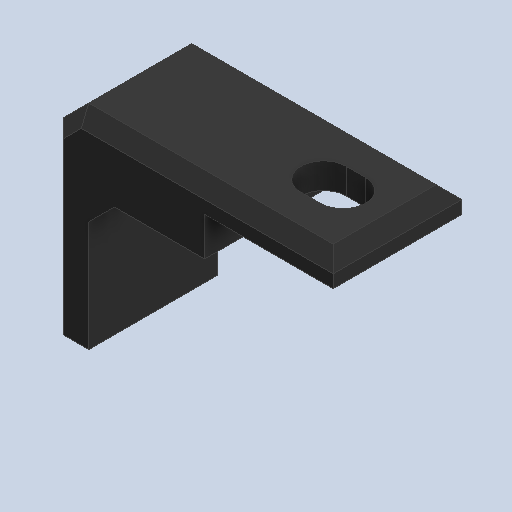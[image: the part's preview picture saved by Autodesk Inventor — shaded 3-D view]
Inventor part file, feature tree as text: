
AUTODESK INVENTOR PART (.ipt)
format: ipt  version: 2024.2 (Build 282272000, 272)  size: 308,736 bytes
history: native  units: mm
features: chamfer x3, extrude x2, sketch x1
ambient origin geometry x8: Origin, YZ Plane, XZ Plane, XY Plane, X Axis, Y Axis, Z Axis, Center Point
bodies: Solid1 (feature_tree)
feature tree (6):
  extrude  "Extrusion1"  Depth=10.0mm
  chamfer  "Chamfer1"  Distance=3.0mm
  extrude  "Extrusion2"  Depth=9.0mm
  chamfer  "Chamfer2"  Distance=3.0mm
  chamfer  "Chamfer3"  Distance=10.6mm
  sketch  "Sketch2"  dims[d0=2.0mm d1=10.0mm d2=3.0mm d3=9.0mm d4=3.0mm d5=10.6mm d6=10.0mm d7=0.0mm d8=2.0mm d9=2.0mm d10=45.0deg d11=1.75mm d12=1.5mm d13=5.0mm d14=0.0mm d15=0.0mm d16=2.0mm d17=2.0mm d18=45.0deg d19=1.0mm d20=2.0mm d21=45.0deg]
